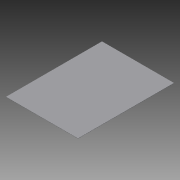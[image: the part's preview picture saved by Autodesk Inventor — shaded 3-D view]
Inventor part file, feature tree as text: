
AUTODESK INVENTOR PART (.ipt)
format: ipt  version: 2015 SP1 (Build 190203100, 203)  size: 69,120 bytes
history: native  units: mm
features: extrude x1, sketch x1
ambient origin geometry x8: Origin, YZ Plane, XZ Plane, XY Plane, X Axis, Y Axis, Z Axis, Center Point
bodies: Solid1 (feature_tree)
feature tree (2):
  extrude  "Extrusion1"  Depth=4000.0mm
  sketch  "Sketch1"  dims[d0=3000.0mm d1=4000.0mm d2=10.0mm d3=0.0mm]
